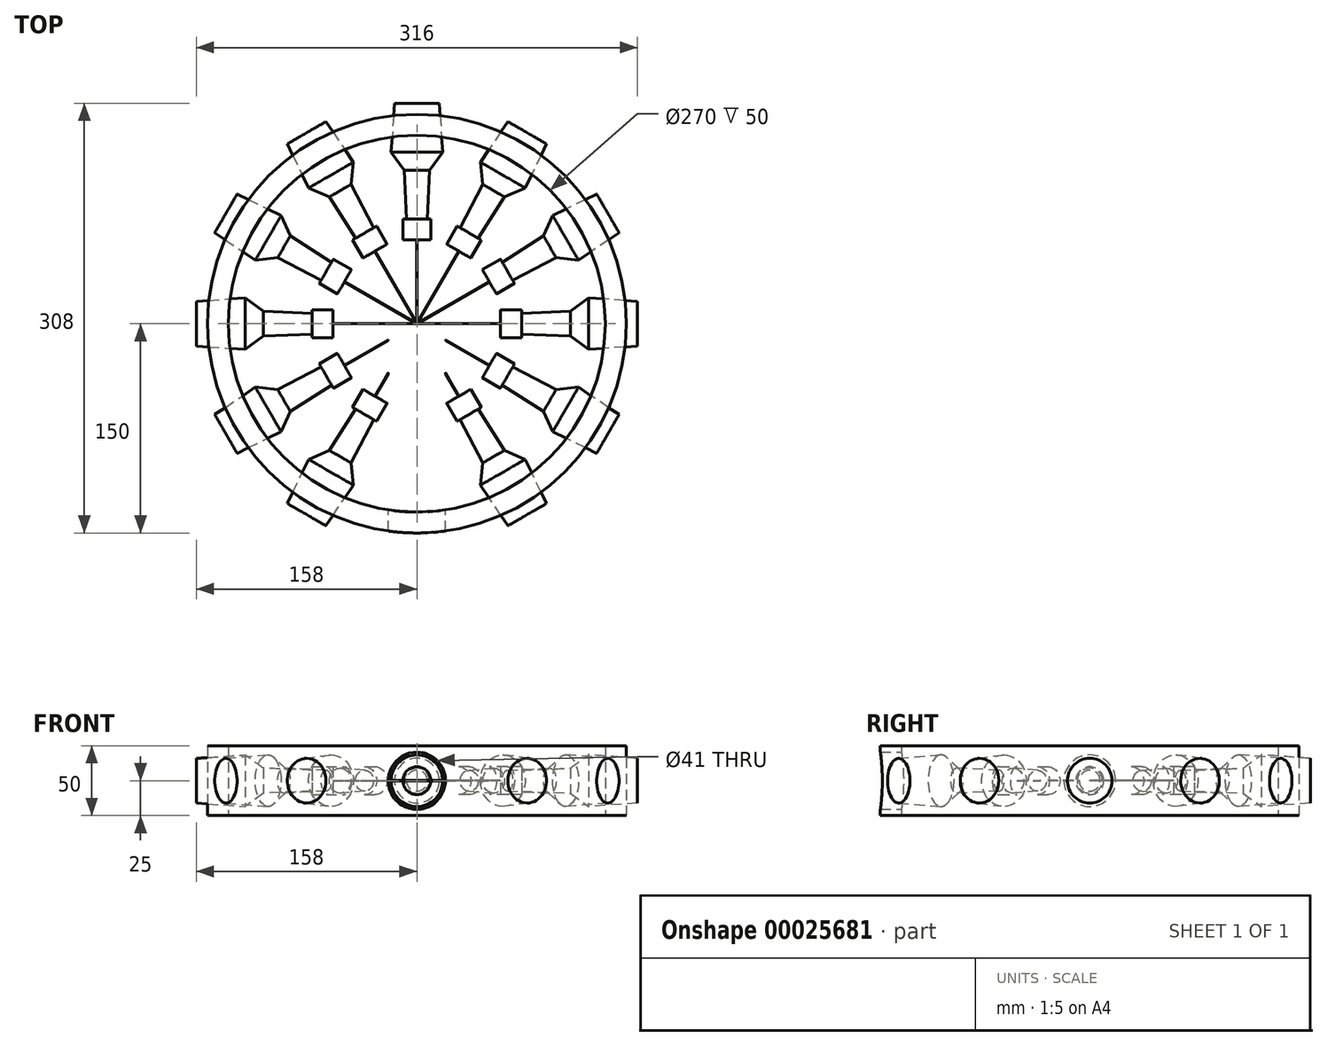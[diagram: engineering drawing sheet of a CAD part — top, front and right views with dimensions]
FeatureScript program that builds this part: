
annotation { "Feature Type Name" : "Feature", "Feature Type Description" : "" }
export const myFeature = defineFeature(function(context is Context, id is Id, definition is map)
    precondition{}
    {
        {
            var Q0;
            Q0=qCreatedBy(makeId("Front.planeOp"),FACE);
            var sketch = newSketch(context, id + "F0", { "sketchPlane" : qUnion([Q0])});
            skLineSegment(sketch, "E0", {"start": v(0, 0) * mm, "end": v(150.85, 0) * mm, "construction": true});
            skLineSegment(sketch, "E1", {"start": v(60, 0.1) * mm, "end": v(60, 10) * mm});
            skLineSegment(sketch, "E2", {"start": v(60, 10) * mm, "end": v(75, 10) * mm});
            skLineSegment(sketch, "E3", {"start": v(110, 9) * mm, "end": v(123, 18.5) * mm});
            skLineSegment(sketch, "E4", {"start": v(123, 18.5) * mm, "end": v(158, 16) * mm});
            skLineSegment(sketch, "E5", {"start": v(158, 16) * mm, "end": v(158, 0) * mm});
            skLineSegment(sketch, "E6", {"start": v(158, 0) * mm, "end": v(60, 0) * mm});
            skLineSegment(sketch, "E7", {"start": v(60, 0.1) * mm, "end": v(0, 0.1) * mm});
            skLineSegment(sketch, "E8", {"start": v(0, 0.1) * mm, "end": v(0, 0) * mm});
            skLineSegment(sketch, "E9", {"start": v(60, 0) * mm, "end": v(0, 0) * mm});
            skLineSegment(sketch, "E10", {"start": v(75, 10) * mm, "end": v(75, 7.5) * mm});
            skLineSegment(sketch, "E11", {"start": v(75, 7.5) * mm, "end": v(110, 9) * mm});
            skLineSegment(sketch, "E12", {"start": v(0, -10) * mm, "end": v(0, 10) * mm, "construction": true});
            skSolve(sketch);
        }
        {
            var Q0;
            Q0 = qSketchRegion(id + "F0", true);
            var Q1;
            Q1=sQuery(id+"F0.wireOp",EDGE,"E0");
            revolve(context, id + "F1", {"entities" : qUnion([Q0]), "axis" : qUnion([Q1]), "revolveType" : RevolveType.FULL});
        }
        {
            var Q0;
            Q0=makeQuery(id+"F1.opRevolve","SWEPT_BODY",BODY,{"disambiguationData":[OSD([sQuery(id+"F0.wireOp",EDGE,"E1"),sQuery(id+"F0.wireOp",EDGE,"E2"),sQuery(id+"F0.wireOp",EDGE,"E3"),sQuery(id+"F0.wireOp",EDGE,"E4"),sQuery(id+"F0.wireOp",EDGE,"E5"),sQuery(id+"F0.wireOp",EDGE,"E6")])]});
            var Q1;
            Q1=sQuery(id+"F0.wireOp",EDGE,"E12");
            circularPattern(context, id + "F2", {"operationType" : NewBodyOperationType.ADD, "entities" : qUnion([Q0]), "axis" : qUnion([Q1]), "angle" : 360 * degree, "instanceCount" : 12, "equalSpace" : true});
        }
        {
            var Q0;
            Q0=qCreatedBy(makeId("Top.planeOp"),FACE);
            var sketch = newSketch(context, id + "F3", { "sketchPlane" : qUnion([Q0])});
            skCircle(sketch, "E13", {"center": v(0, 0) * mm, "radius": 150 * mm});
            skCircle(sketch, "E14", {"center": v(0, 0) * mm, "radius": 135 * mm});
            skSolve(sketch);
        }
        {
            var Q0;
            Q0 = qSketchRegion(id + "F3", true);
            extrude(context, id + "F4", {"entities" : qUnion([Q0]), "endBound" : BoundingType.SYMMETRIC, "depth" : 50 * mm, "offsetDistance" : 25 * mm});
        }
        {
            var Q0;
            Q0=qCreatedBy(makeId("Front.planeOp"),FACE);
            var sketch = newSketch(context, id + "F5", { "sketchPlane" : qUnion([Q0])});
            skCircle(sketch, "E15.0", {"center": v(0, 0) * mm, "radius": 20.5 * mm});
            skSolve(sketch);
        }
        {
            var Q0;
            Q0 = qSketchRegion(id + "F5", true);
            extrude(context, id + "F6", {"entities" : qUnion([Q0]), "operationType" : NewBodyOperationType.REMOVE, "endBound" : BoundingType.THROUGH_ALL, "depth" : 25 * mm, "offsetDistance" : 25 * mm});
        }
    });
